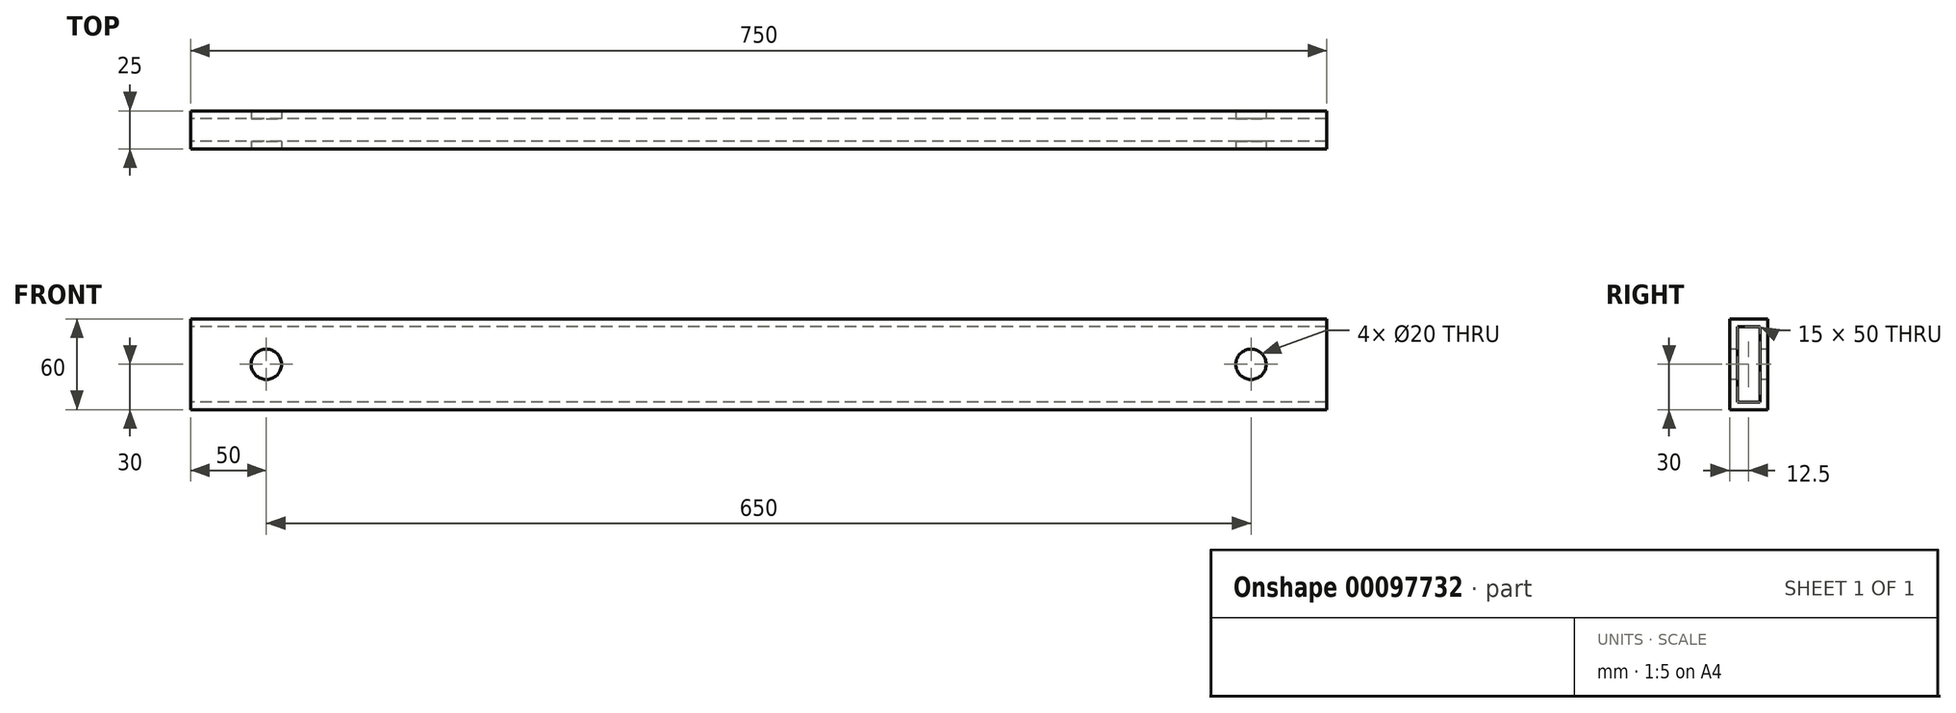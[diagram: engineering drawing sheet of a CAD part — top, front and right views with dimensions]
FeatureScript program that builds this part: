
annotation { "Feature Type Name" : "Feature", "Feature Type Description" : "" }
export const myFeature = defineFeature(function(context is Context, id is Id, definition is map)
    precondition{}
    {
        {
            var Q0;
            Q0=qCreatedBy(makeId("Right.planeOp"),FACE);
            var sketch = newSketch(context, id + "F0", { "sketchPlane" : qUnion([Q0])});
            skLineSegment(sketch, "E0.bottom", {"start": v(12.5, -30) * mm, "end": v(-12.5, -30) * mm});
            skLineSegment(sketch, "E0.top", {"start": v(12.5, 30) * mm, "end": v(-12.5, 30) * mm});
            skLineSegment(sketch, "E0.left", {"start": v(12.5, -30) * mm, "end": v(12.5, 30) * mm});
            skLineSegment(sketch, "E0.right", {"start": v(-12.5, -30) * mm, "end": v(-12.5, 30) * mm});
            skPoint(sketch, "E0.middle", {"position": v(0, 0) * mm});
            skLineSegment(sketch, "E1.bottom", {"start": v(7.5, -25) * mm, "end": v(-7.5, -25) * mm});
            skLineSegment(sketch, "E1.top", {"start": v(7.5, 25) * mm, "end": v(-7.5, 25) * mm});
            skLineSegment(sketch, "E1.left", {"start": v(7.5, -25) * mm, "end": v(7.5, 25) * mm});
            skLineSegment(sketch, "E1.right", {"start": v(-7.5, -25) * mm, "end": v(-7.5, 25) * mm});
            skSolve(sketch);
        }
        {
            var Q0;
            Q0=makeQuery(id+"F0.imprint","IMPRINT",FACE,{"disambiguationData":[TD([[makeQuery(id+"F0.imprint","IMPRINT",EDGE,{"derivedFrom":sQuery(id+"F0.wireOp",EDGE,"E0.bottom")}),-1.0]])]});
            extrude(context, id + "F1", {"entities" : qUnion([Q0]), "endBound" : BoundingType.SYMMETRIC, "depth" : 750 * mm});
        }
        {
            var Q0;
            Q0=makeQuery(id+"F1.opExtrude","SWEPT_FACE",FACE,{"disambiguationData":[OSD([sQuery(id+"F0.wireOp",EDGE,"E0.right")])]});
            var sketch = newSketch(context, id + "F2", { "sketchPlane" : qUnion([Q0])});
            skCircle(sketch, "E2", {"center": v(-325, 0) * mm, "radius": 10 * mm});
            skCircle(sketch, "E3", {"center": v(325, 0) * mm, "radius": 10 * mm});
            skSolve(sketch);
        }
        {
            var Q0;
            Q0=makeQuery(id+"F2.imprint","IMPRINT",FACE,{"disambiguationData":[TD([[makeQuery(id+"F2.imprint","IMPRINT",EDGE,{"derivedFrom":sQuery(id+"F2.wireOp",EDGE,"E2")}),1.0]])]});
            var Q1;
            Q1=makeQuery(id+"F2.imprint","IMPRINT",FACE,{"disambiguationData":[TD([[makeQuery(id+"F2.imprint","IMPRINT",EDGE,{"derivedFrom":sQuery(id+"F2.wireOp",EDGE,"E3")}),1.0]])]});
            extrude(context, id + "F3", {"entities" : qUnion([Q0, Q1]), "operationType" : NewBodyOperationType.REMOVE, "endBound" : BoundingType.THROUGH_ALL, "oppositeDirection" : true, "depth" : 25 * mm});
        }
    });
